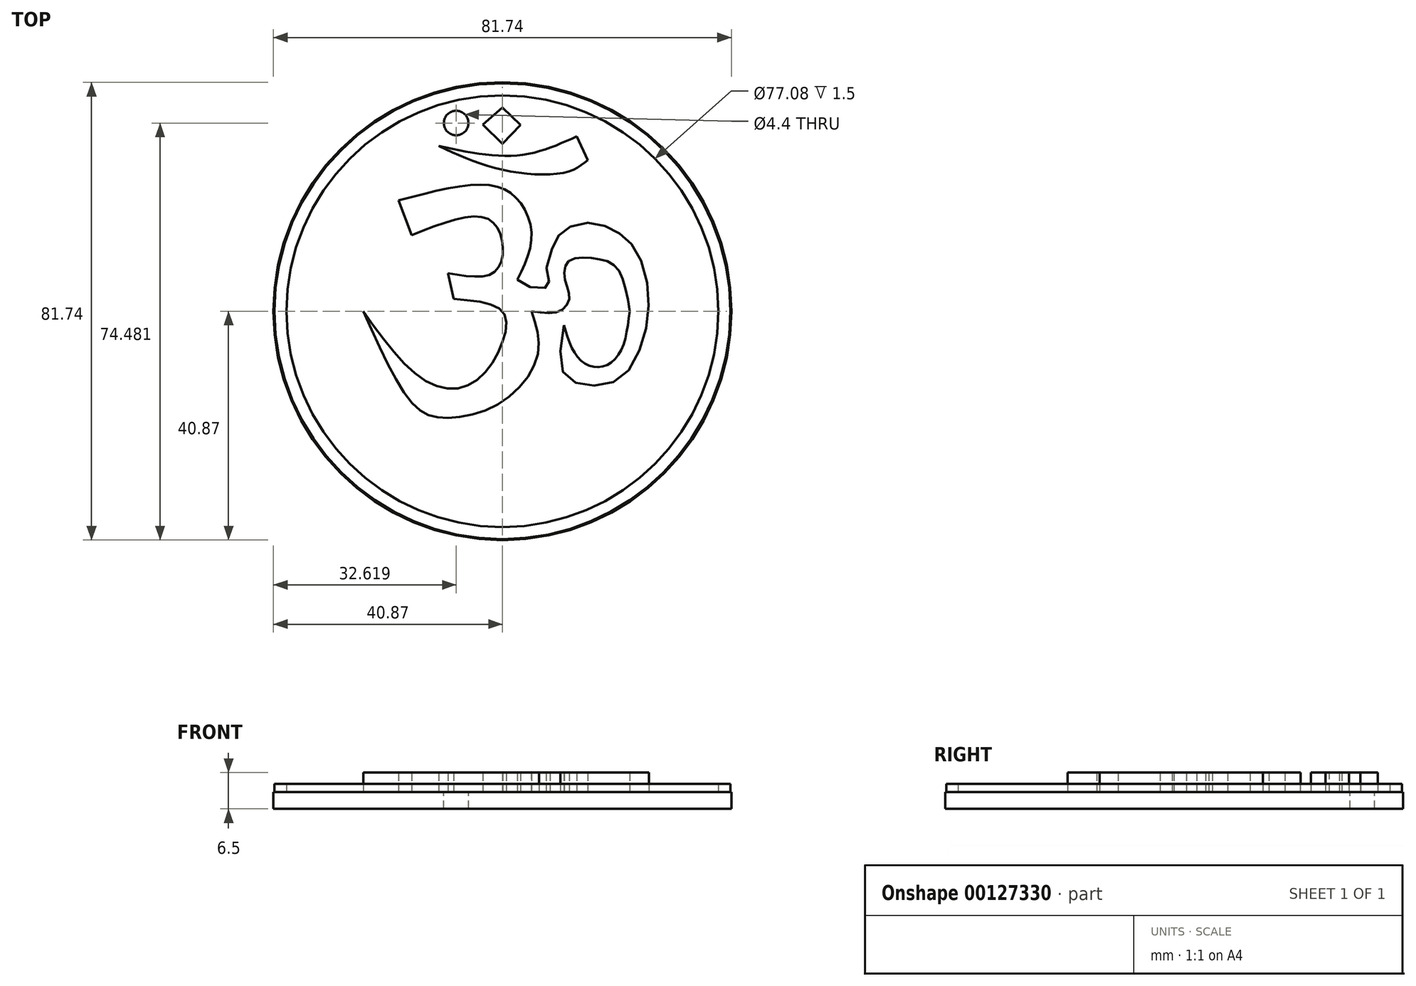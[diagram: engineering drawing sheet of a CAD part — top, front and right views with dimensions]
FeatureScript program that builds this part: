
annotation { "Feature Type Name" : "Feature", "Feature Type Description" : "" }
export const myFeature = defineFeature(function(context is Context, id is Id, definition is map)
    precondition{}
    {
        {
            var Q0;
            Q0=qCreatedBy(makeId("Top.planeOp"),FACE);
            var sketch = newSketch(context, id + "F0", { "sketchPlane" : qUnion([Q0])});
            skCircle(sketch, "E0", {"center": v(0, 0) * mm, "radius": 40.87 * mm});
            skSolve(sketch);
        }
        {
            var Q0;
            Q0=makeQuery(id+"F0.imprint","IMPRINT",FACE,{"disambiguationData":[TD([[makeQuery(id+"F0.imprint","IMPRINT",EDGE,{"derivedFrom":sQuery(id+"F0.wireOp",EDGE,"E0")}),1.0]])]});
            extrude(context, id + "F1", {"entities" : qUnion([Q0]), "depth" : 3 * mm});
        }
        {
            var Q0;
            Q0=makeQuery(id+"F1.opExtrude","CAP_FACE",FACE,{"disambiguationData":[OSD([sQuery(id+"F0.wireOp",EDGE,"E0")])],"isStart":false});
            var sketch = newSketch(context, id + "F2", { "sketchPlane" : qUnion([Q0])});
            skCircle(sketch, "E1", {"center": v(0, 0) * mm, "radius": 40.7 * mm});
            skCircle(sketch, "E2", {"center": v(0, 0) * mm, "radius": 38.54 * mm});
            skSolve(sketch);
        }
        {
            var Q0;
            Q0 = qSketchRegion(id + "F2", true);
            extrude(context, id + "F3", {"entities" : qUnion([Q0]), "operationType" : NewBodyOperationType.ADD, "depth" : 1.5 * mm});
        }
        {
            var Q0;
            Q0=makeQuery(id+"F1.opExtrude","CAP_FACE",FACE,{"disambiguationData":[OSD([sQuery(id+"F0.wireOp",EDGE,"E0")])],"isStart":false});
            var sketch = newSketch(context, id + "F4", { "sketchPlane" : qUnion([Q0])});
            skLineSegment(sketch, "E3", {"start": v(-18.52, 19.8) * mm, "end": v(-16.2, 13.59) * mm});
            skPoint(sketch, "E4.1.internal.snap0", {"position": v(-17.36, 16.69) * mm});
            skFitSpline(sketch, "E4", {"points": [v(-16.2, 13.59) * mm, v(-3.08, 16.69) * mm, v(0, 12.29) * mm, v(-1.49, 6.95) * mm, v(-9.71, 6.8) * mm], "startDerivative": vector(46.84, 18.58) * mm, "endDerivative": vector(-38.15, 6.56) * mm});
            skLineSegment(sketch, "E5", {"start": v(-9.71, 6.8) * mm, "end": v(-8.7, 2.19) * mm});
            skFitSpline(sketch, "E6", {"points": [v(-8.7, 2.19) * mm, v(0, 0) * mm, v(0, -5.56) * mm, v(-5.4, -12.88) * mm, v(-13.3, -12.68) * mm, v(-24.85, 0) * mm], "startDerivative": vector(56.04, -4.45) * mm, "endDerivative": vector(-41.8, 58.3) * mm});
            skFitSpline(sketch, "E7", {"points": [v(-24.85, 0) * mm, v(-15.8, -16.73) * mm, v(-10.2, -19.04) * mm, v(0, -16.15) * mm, v(6.36, -7.48) * mm, v(5.2, 0) * mm], "startDerivative": vector(33.64, -75.64) * mm, "endDerivative": vector(-14.58, 42.63) * mm});
            skFitSpline(sketch, "E8", {"points": [v(-18.52, 19.8) * mm, v(-2.89, 22.56) * mm, v(2.89, 19.8) * mm, v(5.2, 13.32) * mm, v(2.7, 5.61) * mm], "startDerivative": vector(52.35, 13.93) * mm, "endDerivative": vector(-15.45, -32.32) * mm});
            skFitSpline(sketch, "E9", {"points": [v(5.2, 0) * mm, v(10.2, 0) * mm, v(11.94, 2.34) * mm, v(11.17, 5.61) * mm, v(11.75, 8.89) * mm, v(16.18, 9.47) * mm, v(20.42, 7.73) * mm, v(22.73, 0) * mm], "startDerivative": vector(36.55, -5.69) * mm, "endDerivative": vector(7.42, -47.73) * mm});
            skFitSpline(sketch, "E10", {"points": [v(22.73, 0) * mm, v(20.8, -7.68) * mm, v(17.14, -9.99) * mm, v(13.48, -8.25) * mm, v(10.98, -2.48) * mm], "startDerivative": vector(-3.55, -29.06) * mm, "endDerivative": vector(-7.24, 24.5) * mm});
            skFitSpline(sketch, "E11", {"points": [v(10.98, -2.48) * mm, v(10.98, -11.14) * mm, v(15.6, -13.26) * mm, v(21.38, -11.72) * mm, v(25.23, -4.65) * mm, v(26, 3.88) * mm, v(23.5, 11.4) * mm, v(20.22, 14.28) * mm, v(15.8, 15.82) * mm, v(10.98, 14.48) * mm, v(9.05, 11.59) * mm, v(7.9, 6.39) * mm, v(8.48, 4.65) * mm, v(5.97, 4.07) * mm, v(2.7, 5.61) * mm], "startDerivative": vector(-18.27, -109.77) * mm, "endDerivative": vector(-50.44, 34.68) * mm});
            skFitSpline(sketch, "E12", {"points": [v(-11.36, 29.5) * mm, v(0, 25.26) * mm, v(11.56, 24.88) * mm, v(15.22, 27) * mm], "startDerivative": vector(27.6, -12.7) * mm, "endDerivative": vector(12.9, 10.8) * mm});
            skFitSpline(sketch, "E13", {"points": [v(-11.36, 29.5) * mm, v(2.89, 27.85) * mm, v(13.3, 31.23) * mm], "startDerivative": vector(27.87, -5.85) * mm, "endDerivative": vector(21.3, 9.67) * mm});
            skLineSegment(sketch, "E14", {"start": v(13.3, 31.23) * mm, "end": v(15.22, 27) * mm});
            skLineSegment(sketch, "E15", {"start": v(-3.5, 33.33) * mm, "end": v(0, 29.92) * mm});
            skLineSegment(sketch, "E16", {"start": v(0, 29.92) * mm, "end": v(3.22, 33.23) * mm});
            skLineSegment(sketch, "E17", {"start": v(3.22, 33.23) * mm, "end": v(0, 36.36) * mm});
            skLineSegment(sketch, "E18", {"start": v(0, 36.36) * mm, "end": v(-3.5, 33.33) * mm});
            skSolve(sketch);
        }
        {
            var Q0;
            Q0 = qSketchRegion(id + "F4", true);
            extrude(context, id + "F5", {"entities" : qUnion([Q0]), "operationType" : NewBodyOperationType.ADD, "depth" : 3.5 * mm});
        }
        {
            var Q0;
            Q0=makeQuery(id+"F3.boolean.opBoolean","SPLIT",FACE,{"disambiguationData":[TD([makeQuery(id+"F3.opExtrude","SWEPT_FACE",FACE,{"disambiguationData":[OSD([sQuery(id+"F2.wireOp",EDGE,"E2")])]})])],"derivedFrom":makeQuery(id+"F1.opExtrude","CAP_FACE",FACE,{"disambiguationData":[OSD([sQuery(id+"F0.wireOp",EDGE,"E0")])],"isStart":false})});
            var sketch = newSketch(context, id + "F6", { "sketchPlane" : qUnion([Q0])});
            skCircle(sketch, "E19", {"center": v(-8.25, 33.61) * mm, "radius": 2.2 * mm});
            skSolve(sketch);
        }
        {
            var Q0;
            Q0 = qSketchRegion(id + "F6", true);
            extrude(context, id + "F7", {"entities" : qUnion([Q0]), "operationType" : NewBodyOperationType.REMOVE, "oppositeDirection" : true, "depth" : 3 * mm});
        }
    });
